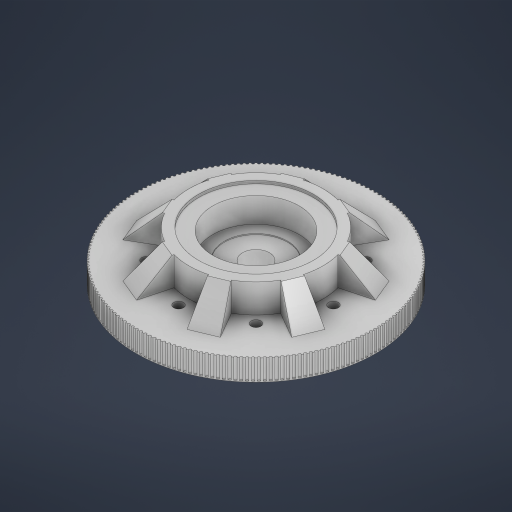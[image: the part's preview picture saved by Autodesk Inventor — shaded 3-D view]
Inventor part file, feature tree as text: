
AUTODESK INVENTOR PART (.ipt)
format: ipt  version: 2024 (Build 280153000, 153)  size: 657,920 bytes
history: native  units: mm
features: extrude x8, sketch x8, pattern_circular x2, chamfer x1, projected_geometry x1
ambient origin geometry x8: Origin, YZ Plane, XZ Plane, XY Plane, X Axis, Y Axis, Z Axis, Center Point
bodies: Solid1 (feature_tree)
feature tree (20):
  extrude  "Extrusion1"  Depth=22.0mm TaperAngle=0.0deg
  extrude  "Extrusion2"  Depth=21.0mm TaperAngle=0.0deg
  extrude  "Extrusion3"  Depth=90.0mm
  pattern_circular  "Circular Pattern1"  Count=14  [1 undecoded]
  extrude  "Extrusion4"  Depth=3.0mm TaperAngle=0.0deg
  extrude  "Extrusion5"  Depth=80.0mm TaperAngle=360.0deg
  extrude  "Extrusion6"  TaperAngle=15.0deg  [1 undecoded]
  extrude  "Extrusion7"  Depth=1.308997mm
  extrude  "Extrusion8"  Depth=30.0mm TaperAngle=0.0deg
  chamfer  "Chamfer1"  Distance=30.0mm Angle=45.0deg
  pattern_circular  "Circular Pattern2"  Count=8 Angle=360.0deg
  sketch  "Sketch1"  dims[d0=250.0mm d1=22.0mm d2=0.0mm]
  sketch  "Sketch2"  dims[d3=30.0mm d4=0.0mm d5=21.0mm d6=0.0mm]
  projected_geometry  "Projected Loop1"
  sketch  "Sketch3"  dims[d7=1800.0mm d8=360.0deg d10=90.0mm d11=140.0mm]
  sketch  "Sketch4"  dims[d12=1.0mm d13=0.0mm d14=3.0mm d15=0.0mm]
  sketch  "Sketch5"  dims[d16=25.0mm d17=0.0mm d18=80.0mm d20=360.0deg]
  sketch  "Sketch6"  dims[d22=20.0mm d23=0.0mm d24=15.0deg]
  sketch  "Sketch7"  dims[d25=60.0deg d26=1.308997mm]
  sketch  "Sketch8"  dims[d27=1.308997mm d28=30.0mm d29=0.0mm d30=30.0mm d31=2.0mm d32=45.0deg d33=80.0mm d34=360.0deg]
note: 2 required parameter values undecoded (feature->parameter linkage not recoverable at this tier; creation-order binding heuristic only, values carry confidence <= 0.55)
